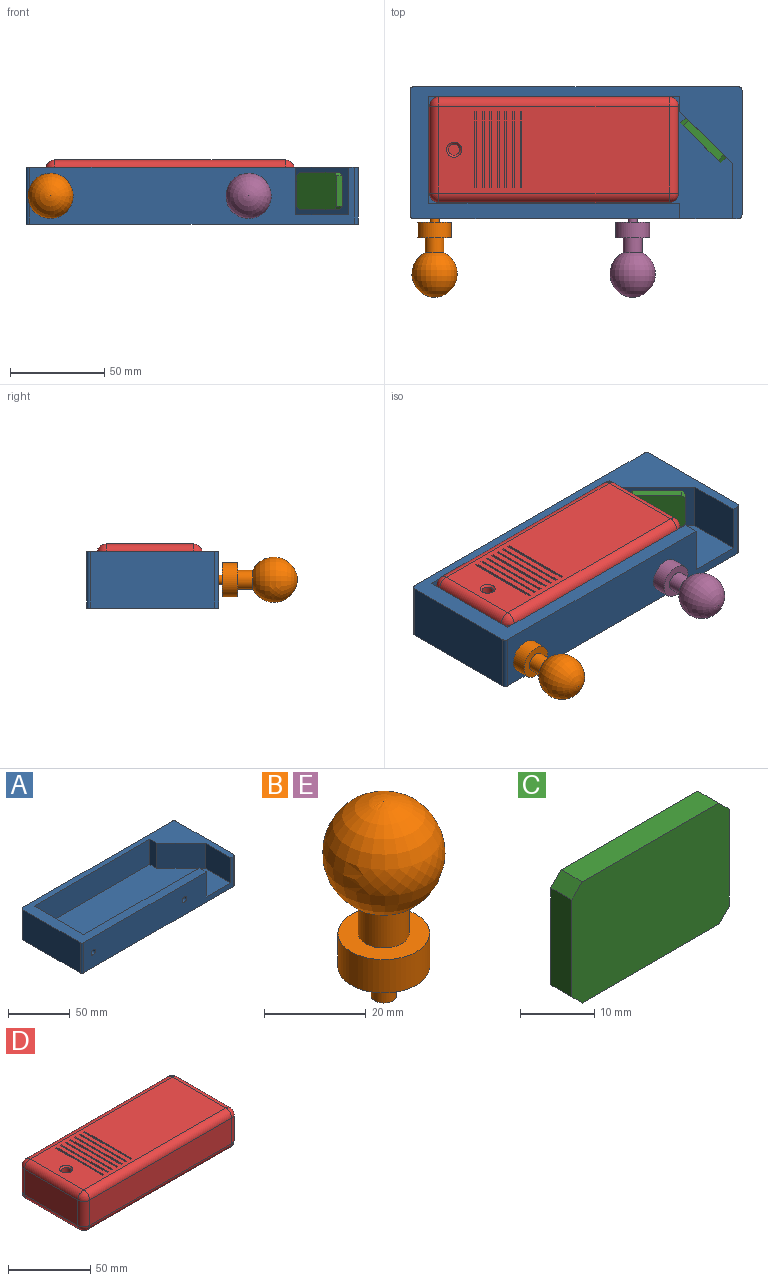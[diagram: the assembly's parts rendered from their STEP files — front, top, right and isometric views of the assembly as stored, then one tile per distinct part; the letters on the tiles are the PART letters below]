
ASSEMBLY  parts=5 mates=4
PART A: 22 faces, bbox 176x70x30 mm
  f0: plane 172x30mm, normal (0,1,0), area 5160mm2, adj f10,f12,f18,f21
  f1: plane 66x30mm, normal (-1,0,0), area 1980mm2, adj f10,f12,f18,f19
  f2: plane 172x30mm, normal (0,-1,0), area 4420.7mm2, adj f7,f10,f11,f12,f13,f14,f16,f19
  f3: plane 57x25mm, normal (1,0,0), area 1425mm2, adj f4,f8,f10,f11
  f4: plane 133x25mm, normal (0,-1,0), area 3325mm2, adj f3,f5,f10,f11
  f5: plane 25x8mm, normal (-1,0,0), area 200mm2, adj f4,f6,f10,f11
  f6: plane 28x28mm, normal (-0.71,-0.71,0), area 989.9mm2, adj f5,f7,f10,f11
  f7: plane 29x25mm, normal (-1,0,0), area 725mm2, adj f2,f6,f10,f11
  f8: plane 133x25mm, normal (0,1,0), area 3325mm2, adj f3,f10,f11,f13
  f9: plane 66x30mm, normal (1,0,0), area 1980mm2, adj f10,f12,f20,f21
  f10: plane 176x70mm, normal (0,0,1), area 3531.6mm2, adj f0,f1,f2,f3,f4,f5,f6,f7
  f11: plane 161x65mm, normal (0,0,1), area 8785mm2, adj f2,f3,f4,f5,f6,f7,f8,f13
  f12: plane 176x70mm, normal (0,0,-1), area 12316.6mm2, adj f0,f1,f2,f9,f18,f19,f20,f21
  f13: plane 25x8mm, normal (1,0,0), area 200mm2, adj f2,f8,f10,f11
  f14: cylinder r=2.5mm len=7mm, axis (0,-1,0), area 110mm2, adj f2,f15
  f15: plane 5x5mm, normal (0,-1,0), area 19.6mm2, adj f14
  f16: cylinder r=2.5mm len=7mm, axis (0,-1,0), area 110mm2, adj f2,f17
  f17: plane 5x5mm, normal (0,-1,0), area 19.6mm2, adj f16
  f18: cylinder r=2mm len=30mm, axis (0,0,1), area 94.2mm2, adj f0,f1,f10,f12
  f19: cylinder r=2mm len=30mm, axis (0,0,-1), area 94.2mm2, adj f1,f2,f10,f12
  f20: cylinder r=2mm len=30mm, axis (0,0,1), area 94.2mm2, adj f2,f9,f10,f12
  f21: cylinder r=2mm len=30mm, axis (0,0,-1), area 94.2mm2, adj f0,f9,f10,f12
PART B: 7 faces, bbox 18x18x23 mm
  f0: plane 18x18mm, normal (0,0,-1), area 234.8mm2, adj f1,f6
  f1: cylinder r=2.5mm len=7mm, axis (0,0,1), area 110mm2, adj f0,f2
  f2: plane 5x5mm, normal (0,0,-1), area 19.6mm2, adj f1
  f3: revolved ~10x5mm, area 0mm2, adj f4
  f4: cylinder r=5mm len=10mm, axis (0,0,1), area 251.3mm2, adj f3,f5
  f5: plane 18x18mm, normal (0,0,1), area 175.9mm2, adj f4,f6
  f6: cylinder r=9mm len=18mm, axis (0,0,1), area 452.4mm2, adj f0,f5
PART C: 10 faces, bbox 30x4x20 mm
  f0: plane 26x4mm, normal (0,0,1), area 104mm2, adj f4,f5,f8,f9
  f1: plane 16x4mm, normal (-1,0,0), area 64mm2, adj f4,f5,f6,f9
  f2: plane 26x4mm, normal (0,0,-1), area 104mm2, adj f4,f5,f6,f7
  f3: plane 16x4mm, normal (1,0,0), area 64mm2, adj f4,f5,f7,f8
  f4: plane 30x20mm, normal (0,-1,0), area 592mm2, adj f0,f1,f2,f3,f6,f7,f8,f9
  f5: plane 30x20mm, normal (0,1,0), area 592mm2, adj f0,f1,f2,f3,f6,f7,f8,f9
  f6: plane 4x2mm, normal (-0.71,0,-0.71), area 11.3mm2, adj f1,f2,f4,f5
  f7: plane 4x2mm, normal (0.71,0,-0.71), area 11.3mm2, adj f2,f3,f4,f5
  f8: plane 4x2mm, normal (0.71,0,0.71), area 11.3mm2, adj f0,f3,f4,f5
  f9: plane 4x2mm, normal (-0.71,0,0.71), area 11.3mm2, adj f0,f1,f4,f5
PART D: 69 faces, bbox 132x56x29 mm
  f0: plane 122x46mm, normal (0,0,1), area 5281.7mm2, adj f15,f18,f19,f22,f31,f32,f33,f34
  f1: plane 122x19mm, normal (0,1,0), area 2318mm2, adj f11,f14,f22,f30
  f2: plane 46x19mm, normal (-1,0,0), area 874mm2, adj f11,f12,f18,f26
  f3: plane 122x19mm, normal (0,-1,0), area 2318mm2, adj f12,f13,f15,f23
  f4: plane 46x19mm, normal (1,0,0), area 607.6mm2, adj f9,f10,f13,f14,f19,f27
  f5: plane 122x46mm, normal (0,0,-1), area 5612mm2, adj f23,f26,f27,f30
  f6: cylinder r=4mm len=8mm, axis (1,0,0), area 62.4mm2, adj f7,f8,f10
  f7: cylinder r=7.5mm len=15mm, axis (1,0,0), area 157.4mm2, adj f6,f8,f9
  f8: plane 19.5x15mm, normal (1,0,0), area 208.5mm2, adj f6,f7
  f9: torus R=8.5mm, axis (1,0,0), area 63.9mm2, adj f4,f7,f10
  f10: torus R=5mm, axis (1,0,0), area 25.8mm2, adj f4,f6,f9
  f11: cylinder r=5mm len=19mm, axis (0,0,1), area 149.2mm2, adj f1,f2,f20,f28
  f12: cylinder r=5mm len=19mm, axis (0,0,-1), area 149.2mm2, adj f2,f3,f16,f24
  f13: cylinder r=5mm len=19mm, axis (0,0,1), area 149.2mm2, adj f3,f4,f17,f25
  f14: cylinder r=5mm len=19mm, axis (0,0,-1), area 149.2mm2, adj f1,f4,f21,f29
  f15: cylinder r=5mm len=122mm, axis (-1,0,0), area 958.2mm2, adj f0,f3,f16,f17
  f16: sphere r=5mm, area 39.3mm2, adj f12,f15,f18
  f17: sphere r=5mm, area 39.3mm2, adj f13,f15,f19
  f18: cylinder r=5mm len=46mm, axis (0,1,0), area 361.3mm2, adj f0,f2,f16,f20
  f19: cylinder r=5mm len=46mm, axis (0,-1,0), area 361.3mm2, adj f0,f4,f17,f21
  f20: sphere r=5mm, area 39.3mm2, adj f11,f18,f22
  f21: sphere r=5mm, area 39.3mm2, adj f14,f19,f22
  f22: cylinder r=5mm len=122mm, axis (1,0,0), area 958.2mm2, adj f0,f1,f20,f21
  f23: cylinder r=5mm len=122mm, axis (1,0,0), area 958.2mm2, adj f3,f5,f24,f25
  f24: sphere r=5mm, area 39.3mm2, adj f12,f23,f26
  f25: sphere r=5mm, area 39.3mm2, adj f13,f23,f27
  f26: cylinder r=5mm len=46mm, axis (0,-1,0), area 361.3mm2, adj f2,f5,f24,f28
  f27: cylinder r=5mm len=46mm, axis (0,1,0), area 361.3mm2, adj f4,f5,f25,f29
  f28: sphere r=5mm, area 39.3mm2, adj f11,f26,f30
  f29: sphere r=5mm, area 39.3mm2, adj f14,f27,f30
  f30: cylinder r=5mm len=122mm, axis (-1,0,0), area 958.2mm2, adj f1,f5,f28,f29
  f31: plane 1x1mm, normal (0,-1,0), area 1mm2, adj f0,f32,f34,f35
  f32: plane 40x1mm, normal (1,0,0), area 40mm2, adj f0,f31,f33,f35
  f33: plane 1x1mm, normal (0,1,0), area 1mm2, adj f0,f32,f34,f35
  f34: plane 40x1mm, normal (-1,0,0), area 40mm2, adj f0,f31,f33,f35
  f35: plane 40x1mm, normal (0,0,1), area 40mm2, adj f31,f32,f33,f34
  f36: plane 1x1mm, normal (0,-1,0), area 1mm2, adj f0,f37,f39,f40
  f37: plane 40x1mm, normal (1,0,0), area 40mm2, adj f0,f36,f38,f40
  f38: plane 1x1mm, normal (0,1,0), area 1mm2, adj f0,f37,f39,f40
  f39: plane 40x1mm, normal (-1,0,0), area 40mm2, adj f0,f36,f38,f40
  f40: plane 40x1mm, normal (0,0,1), area 40mm2, adj f36,f37,f38,f39
  f41: plane 1x1mm, normal (0,-1,0), area 1mm2, adj f0,f42,f44,f45
  f42: plane 40x1mm, normal (1,0,0), area 40mm2, adj f0,f41,f43,f45
  f43: plane 1x1mm, normal (0,1,0), area 1mm2, adj f0,f42,f44,f45
  f44: plane 40x1mm, normal (-1,0,0), area 40mm2, adj f0,f41,f43,f45
  f45: plane 40x1mm, normal (0,0,1), area 40mm2, adj f41,f42,f43,f44
  f46: plane 40x1mm, normal (1,0,0), area 40mm2, adj f0,f47,f49,f50
  f47: plane 1x1mm, normal (0,1,0), area 1mm2, adj f0,f46,f48,f50
  f48: plane 40x1mm, normal (-1,0,0), area 40mm2, adj f0,f47,f49,f50
  f49: plane 1x1mm, normal (0,-1,0), area 1mm2, adj f0,f46,f48,f50
  f50: plane 40x1mm, normal (0,0,1), area 40mm2, adj f46,f47,f48,f49
  f51: plane 1x1mm, normal (0,-1,0), area 1mm2, adj f0,f52,f54,f55
  f52: plane 40x1mm, normal (1,0,0), area 40mm2, adj f0,f51,f53,f55
  f53: plane 1x1mm, normal (0,1,0), area 1mm2, adj f0,f52,f54,f55
  f54: plane 40x1mm, normal (-1,0,0), area 40mm2, adj f0,f51,f53,f55
  f55: plane 40x1mm, normal (0,0,1), area 40mm2, adj f51,f52,f53,f54
  f56: plane 40x1mm, normal (1,0,0), area 40mm2, adj f0,f57,f59,f60
  f57: plane 1x1mm, normal (0,1,0), area 1mm2, adj f0,f56,f58,f60
  f58: plane 40x1mm, normal (-1,0,0), area 40mm2, adj f0,f57,f59,f60
  f59: plane 1x1mm, normal (0,-1,0), area 1mm2, adj f0,f56,f58,f60
  f60: plane 40x1mm, normal (0,0,1), area 40mm2, adj f56,f57,f58,f59
  f61: plane 40x1mm, normal (1,0,0), area 40mm2, adj f0,f62,f64,f65
  f62: plane 1x1mm, normal (0,1,0), area 1mm2, adj f0,f61,f63,f65
  f63: plane 40x1mm, normal (-1,0,0), area 40mm2, adj f0,f62,f64,f65
  f64: plane 1x1mm, normal (0,-1,0), area 1mm2, adj f0,f61,f63,f65
  f65: plane 40x1mm, normal (0,0,1), area 40mm2, adj f61,f62,f63,f64
  f66: cylinder r=3mm len=6mm, axis (0,0,1), area 75.4mm2, adj f67,f68
  f67: plane 6x6mm, normal (0,0,1), area 28.3mm2, adj f66
  f68: cone r=3mm half-angle=45deg, axis (0,0,1), area 31.1mm2, adj f0,f66
PART E: same geometry as B
PLACE A t=(-37.48,-5.75,9.39)mm
PLACE B rot(axis=(1,0,0),90deg) t=(-110.66,-50.03,19.39)mm
PLACE C rot(axis=(0.92,-0.38,0),180deg) t=(34.84,0.01,21.89)mm
PLACE D t=(-10.21,29.24,9.39)mm
PLACE E rot(axis=(1,0,0),90deg) t=(-5.66,-50.03,19.39)mm
MATE fastened B.f1 <-> A.f16  axis (0,1,0) through (-106.33,-35.16,19.39)mm
MATE fastened C.f4 <-> A.f6  axis (0.71,0.71,0) through (37.67,2.84,21.89)mm
MATE fastened D.f5 <-> A.f11  axis (0,0,-1) through (-43,-3.62,9.39)mm
MATE fastened E.f1 <-> A.f14  axis (0,1,0) through (-1.33,-35.16,19.39)mm
